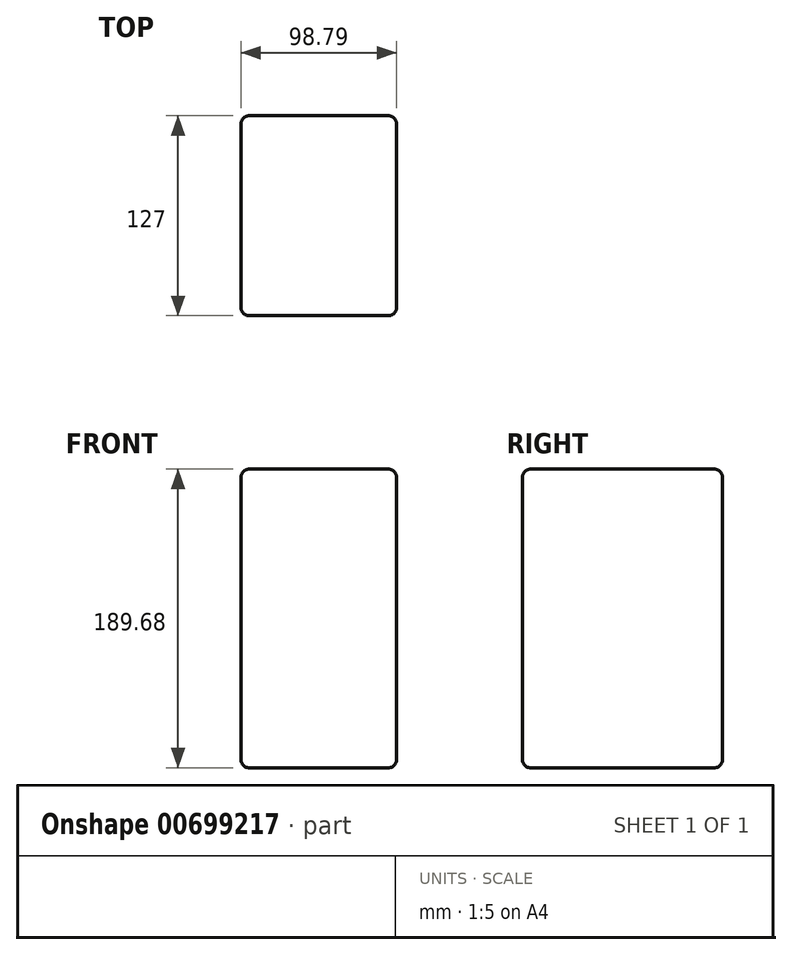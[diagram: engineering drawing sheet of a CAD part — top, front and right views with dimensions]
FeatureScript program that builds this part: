
annotation { "Feature Type Name" : "Feature", "Feature Type Description" : "" }
export const myFeature = defineFeature(function(context is Context, id is Id, definition is map)
    precondition{}
    {
        {
            var Q0;
            Q0=qCreatedBy(makeId("Front.planeOp"),FACE);
            var sketch = newSketch(context, id + "F0", { "sketchPlane" : qUnion([Q0])});
            skLineSegment(sketch, "E0.bottom", {"start": v(11.9, -53.62) * mm, "end": v(-86.9, -53.62) * mm});
            skLineSegment(sketch, "E0.top", {"start": v(11.9, 136.06) * mm, "end": v(-86.9, 136.06) * mm});
            skLineSegment(sketch, "E0.left", {"start": v(11.9, -53.62) * mm, "end": v(11.9, 136.06) * mm});
            skLineSegment(sketch, "E0.right", {"start": v(-86.9, -53.62) * mm, "end": v(-86.9, 136.06) * mm});
            skSolve(sketch);
        }
        {
            var Q0;
            Q0=makeQuery(id+"F0.imprint","IMPRINT",FACE,{"disambiguationData":[TD([[makeQuery(id+"F0.imprint","IMPRINT",EDGE,{"derivedFrom":sQuery(id+"F0.wireOp",EDGE,"E0.bottom")}),-1.0]])]});
            extrude(context, id + "F1", {"entities" : qUnion([Q0]), "depth" : 127 * mm, "offsetDistance" : 25.4 * mm});
        }
        {
            var Q0;
            Q0=makeQuery(id+"F1.opExtrude","SWEPT_EDGE",EDGE,{"disambiguationData":[OSD([sQuery(id+"F0.wireOp",EDGE,"E0.top"),sQuery(id+"F0.wireOp",EDGE,"E0.left")])]});
            fillet(context, id + "F2", {"entities" : qUnion([Q0]), "radius" : 5.08 * mm, "tangentPropagation" : true, "allowEdgeOverflow" : false});
        }
        {
            var Q0;
            Q0=makeQuery(id+"F1.opExtrude","CAP_EDGE",EDGE,{"disambiguationData":[OSD([sQuery(id+"F0.wireOp",EDGE,"E0.bottom")])],"isStart":true});
            fillet(context, id + "F3", {"entities" : qUnion([Q0]), "radius" : 5.08 * mm, "tangentPropagation" : true, "allowEdgeOverflow" : false});
        }
        {
            var Q0;
            Q0=makeQuery(id+"F1.opExtrude","CAP_EDGE",EDGE,{"disambiguationData":[OSD([sQuery(id+"F0.wireOp",EDGE,"E0.right")])],"isStart":true});
            fillet(context, id + "F4", {"entities" : qUnion([Q0]), "radius" : 5.08 * mm, "tangentPropagation" : true, "allowEdgeOverflow" : false});
        }
        {
            var Q0;
            Q0=makeQuery(id+"F1.opExtrude","CAP_EDGE",EDGE,{"disambiguationData":[OSD([sQuery(id+"F0.wireOp",EDGE,"E0.right")])],"isStart":false});
            fillet(context, id + "F5", {"entities" : qUnion([Q0]), "radius" : 5.08 * mm, "tangentPropagation" : true, "allowEdgeOverflow" : false});
        }
        {
            var Q0;
            Q0=makeQuery(id+"F1.opExtrude","SWEPT_EDGE",EDGE,{"disambiguationData":[OSD([sQuery(id+"F0.wireOp",EDGE,"E0.bottom"),sQuery(id+"F0.wireOp",EDGE,"E0.left")])]});
            fillet(context, id + "F6", {"entities" : qUnion([Q0]), "radius" : 5.08 * mm, "tangentPropagation" : true, "allowEdgeOverflow" : false});
        }
    });
